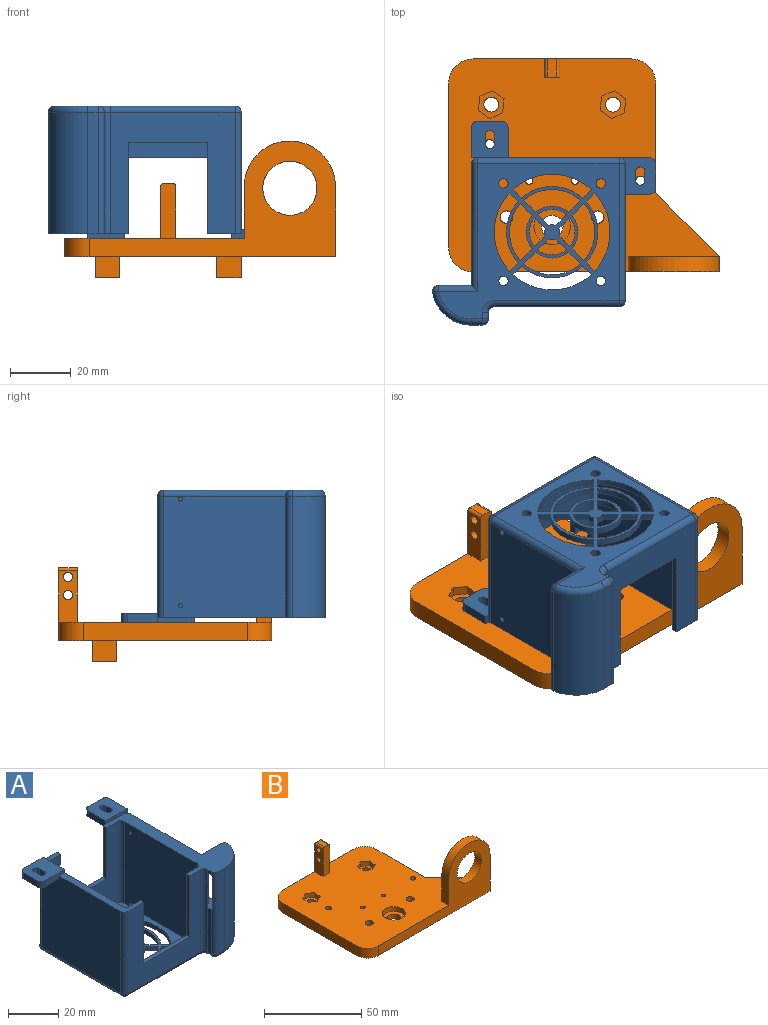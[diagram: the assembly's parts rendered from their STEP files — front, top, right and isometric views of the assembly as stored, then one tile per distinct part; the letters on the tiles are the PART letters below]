
ASSEMBLY  parts=2 mates=1
PART A: 150 faces, bbox 74.3x68.1x43.5 mm
  f0: plane 37x11mm, normal (0,0,1), area 127mm2, adj f2,f5,f73,f76,f84,f85,f121,f130
  f1: plane 7.89x3.33mm, normal (0,0,1), area 16.5mm2, adj f3,f8,f9,f119,f131
  f2: plane 41x40mm, normal (1,0,0), area 1628mm2, adj f0,f3,f70,f76,f130,f137
  f3: cylinder r=2mm len=40mm, axis (0,0,-1), area 113.9mm2, adj f1,f2,f6,f8,f70,f124,f131,f137
  f4: cylinder r=2mm len=38.5mm, axis (0,0,-1), area 121mm2, adj f5,f9,f109,f126
  f5: plane 45x40mm, normal (-1,0,0), area 1785mm2, adj f0,f4,f84,f107,f126,f130
  f6: plane 40x38mm, normal (0,-1,0), area 775.8mm2, adj f3,f7,f10,f70,f74,f117,f118,f123
  f7: plane 9x2mm, normal (1,0,0), area 18mm2, adj f6,f9,f117,f123
  f8: plane 6.5x6mm, normal (0,-1,0), area 31.8mm2, adj f1,f3,f119,f124,f125
  f9: plane 56.5x41.5mm, normal (0,1,0), area 1154.7mm2, adj f1,f4,f7,f10,f83,f111,f117,f118
  f10: plane 55x26.32mm, normal (0,0,1), area 467mm2, adj f6,f9,f15,f17,f72,f73,f74,f75
  f11: plane 11.87x1.77mm, normal (0,0,-1), area 21mm2, adj f12,f15,f81,f92,f94,f96
  f12: plane 31x11.54mm, normal (1,0,0), area 154.7mm2, adj f11,f88,f93,f94,f96,f100
  f13: plane 31x0.04mm, normal (0,1,0), area 1.2mm2, adj f91,f92,f93,f99
  f14: plane 10.82x2mm, normal (0,1,0), area 21.6mm2, adj f15,f82,f93,f116
  f15: cylinder r=2mm len=40mm, axis (0,0,-1), area 118.7mm2, adj f10,f11,f14,f80,f81,f92,f93,f114
  f16: plane 21.5x2mm, normal (-1,0,0), area 43mm2, adj f17,f77,f88,f106
  f17: cylinder r=2mm len=40mm, axis (0,0,-1), area 117.1mm2, adj f10,f16,f78,f79,f86,f87,f88,f108
  f18: plane 3.9x3.9mm, normal (0.71,0.71,0), area 11mm2, adj f19,f69,f70,f71
  f19: cylinder r=14mm len=18.71mm, axis (0,0,-1), area 41mm2, adj f18,f20,f70,f71
  f20: plane 3.9x3.9mm, normal (-0.71,0.71,0), area 11mm2, adj f19,f69,f70,f71
  f21: plane 2.83x2.83mm, normal (-0.71,0.71,0), area 8mm2, adj f22,f54,f70,f71
  f22: cylinder r=19mm len=25.79mm, axis (0,0,-1), area 56.7mm2, adj f21,f23,f70,f71
  f23: plane 2.83x2.83mm, normal (-0.71,-0.71,0), area 8mm2, adj f22,f54,f70,f71
  f24: plane 3.9x3.9mm, normal (-0.71,0.71,0), area 11mm2, adj f25,f55,f70,f71
  f25: cylinder r=14mm len=18.71mm, axis (0,0,-1), area 41mm2, adj f24,f26,f70,f71
  f26: plane 3.9x3.9mm, normal (-0.71,-0.71,0), area 11mm2, adj f25,f55,f70,f71
  f27: plane 3.9x3.9mm, normal (-0.71,-0.71,0), area 11mm2, adj f28,f56,f70,f71
  f28: cylinder r=14mm len=18.71mm, axis (0,0,-1), area 41mm2, adj f27,f29,f70,f71
  f29: plane 3.9x3.9mm, normal (0.71,-0.71,0), area 11mm2, adj f28,f56,f70,f71
  f30: cylinder r=15mm len=20.13mm, axis (0,0,-1), area 44.1mm2, adj f31,f61,f70,f71
  f31: plane 2.83x2.83mm, normal (-0.71,-0.71,0), area 8mm2, adj f30,f32,f70,f71
  f32: cylinder r=19mm len=25.79mm, axis (0,0,-1), area 56.7mm2, adj f31,f61,f70,f71
  f33: cylinder r=8.5mm len=10.91mm, axis (0,0,-1), area 23.7mm2, adj f34,f62,f70,f71
  f34: plane 3.9x3.9mm, normal (0.71,-0.71,0), area 11mm2, adj f33,f35,f70,f71
  f35: cylinder r=14mm len=18.71mm, axis (0,0,-1), area 41mm2, adj f34,f62,f70,f71
  f36: cylinder r=2.5mm len=2.31mm, axis (0,0,-1), area 4.8mm2, adj f37,f63,f70,f71
  f37: plane 3.59x3.59mm, normal (-0.71,0.71,0), area 10.2mm2, adj f36,f38,f70,f71
  f38: cylinder r=7.5mm len=9.49mm, axis (0,0,-1), area 20.6mm2, adj f37,f63,f70,f71
  f39: cylinder r=15mm len=20.13mm, axis (0,0,-1), area 44.1mm2, adj f40,f64,f70,f71
  f40: plane 2.83x2.83mm, normal (0.71,0.71,0), area 8mm2, adj f39,f41,f70,f71
  f41: cylinder r=19mm len=25.79mm, axis (0,0,-1), area 56.7mm2, adj f40,f64,f70,f71
  f42: cylinder r=2.5mm len=2.31mm, axis (0,0,-1), area 4.8mm2, adj f43,f65,f70,f71
  f43: plane 3.59x3.59mm, normal (0.71,0.71,0), area 10.2mm2, adj f42,f44,f70,f71
  f44: cylinder r=7.5mm len=9.49mm, axis (0,0,-1), area 20.6mm2, adj f43,f65,f70,f71
  f45: cylinder r=15mm len=20.13mm, axis (0,0,-1), area 44.1mm2, adj f46,f66,f70,f71
  f46: plane 2.83x2.83mm, normal (0.71,-0.71,0), area 8mm2, adj f45,f47,f70,f71
  f47: cylinder r=19mm len=25.79mm, axis (0,0,-1), area 56.7mm2, adj f46,f66,f70,f71
  f48: cylinder r=2.5mm len=2.31mm, axis (0,0,-1), area 4.8mm2, adj f49,f67,f70,f71
  f49: plane 3.59x3.59mm, normal (0.71,-0.71,0), area 10.2mm2, adj f48,f50,f70,f71
  f50: cylinder r=7.5mm len=9.49mm, axis (0,0,-1), area 20.6mm2, adj f49,f67,f70,f71
  f51: cylinder r=2.5mm len=2.31mm, axis (0,0,-1), area 4.8mm2, adj f52,f68,f70,f71
  f52: plane 3.59x3.59mm, normal (-0.71,-0.71,0), area 10.2mm2, adj f51,f53,f70,f71
  f53: cylinder r=7.5mm len=9.49mm, axis (0,0,-1), area 20.6mm2, adj f52,f68,f70,f71
  f54: cylinder r=15mm len=20.13mm, axis (0,0,-1), area 44.1mm2, adj f21,f23,f70,f71
  f55: cylinder r=8.5mm len=10.91mm, axis (0,0,-1), area 23.7mm2, adj f24,f26,f70,f71
  f56: cylinder r=8.5mm len=10.91mm, axis (0,0,-1), area 23.7mm2, adj f27,f29,f70,f71
  f57: cylinder r=1.55mm len=3.1mm, axis (0,0,-1), area 19.5mm2, adj f70,f71
  f58: cylinder r=1.55mm len=3.1mm, axis (0,0,-1), area 19.5mm2, adj f70,f71
  f59: cylinder r=1.55mm len=3.1mm, axis (0,0,-1), area 19.5mm2, adj f70,f71
  f60: cylinder r=1.55mm len=3.1mm, axis (0,0,-1), area 19.5mm2, adj f70,f71
  f61: plane 2.83x2.83mm, normal (0.71,-0.71,0), area 8mm2, adj f30,f32,f70,f71
  f62: plane 3.9x3.9mm, normal (0.71,0.71,0), area 11mm2, adj f33,f35,f70,f71
  f63: plane 3.59x3.59mm, normal (-0.71,-0.71,0), area 10.2mm2, adj f36,f38,f70,f71
  f64: plane 2.83x2.83mm, normal (-0.71,0.71,0), area 8mm2, adj f39,f41,f70,f71
  f65: plane 3.59x3.59mm, normal (-0.71,0.71,0), area 10.2mm2, adj f42,f44,f70,f71
  f66: plane 2.83x2.83mm, normal (0.71,0.71,0), area 8mm2, adj f45,f47,f70,f71
  f67: plane 3.59x3.59mm, normal (0.71,0.71,0), area 10.2mm2, adj f48,f50,f70,f71
  f68: plane 3.59x3.59mm, normal (0.71,-0.71,0), area 10.2mm2, adj f51,f53,f70,f71
  f69: cylinder r=8.5mm len=10.91mm, axis (0,0,-1), area 23.7mm2, adj f18,f20,f70,f71
  f70: plane 45x42mm, normal (0,0,1), area 970.5mm2, adj f2,f3,f6,f18,f19,f20,f21,f22
  f71: plane 59.32x51mm, normal (0,0,-1), area 1280mm2, adj f18,f19,f20,f21,f22,f23,f24,f25
  f72: plane 41x40mm, normal (-1,0,0), area 1636.9mm2, adj f10,f70,f74,f75,f101,f102
  f73: plane 40x38mm, normal (0,1,0), area 740mm2, adj f0,f10,f70,f75,f76,f120,f121,f122
  f74: cylinder r=2mm len=40mm, axis (0,0,-1), area 125.7mm2, adj f6,f10,f70,f72
  f75: cylinder r=2mm len=40mm, axis (0,0,-1), area 125.7mm2, adj f10,f70,f72,f73
  f76: cylinder r=2mm len=40mm, axis (0,0,-1), area 125.7mm2, adj f0,f2,f70,f73
  f77: cylinder r=2mm len=40mm, axis (0,0,-1), area 125.7mm2, adj f10,f16,f78,f85,f90,f104
  f78: plane 2x1.5mm, normal (-1,0,0), area 3mm2, adj f10,f17,f77,f87
  f79: plane 40x3.5mm, normal (0,-1,0), area 140mm2, adj f10,f17,f80,f110
  f80: cylinder r=13mm len=40mm, axis (0,0,-1), area 721.7mm2, adj f10,f15,f79,f112
  f81: plane 10.82x7mm, normal (0,1,0), area 75.7mm2, adj f10,f11,f15,f82
  f82: plane 40x40mm, normal (1,0,0), area 1596.9mm2, adj f10,f14,f81,f83,f94,f101,f102,f115
  f83: cylinder r=2mm len=40mm, axis (0,0,-1), area 125.7mm2, adj f9,f10,f82,f113,f141
  f84: cylinder r=2mm len=40mm, axis (0,0,-1), area 125.7mm2, adj f0,f5,f85,f105
  f85: plane 41x40mm, normal (0,-1,0), area 860mm2, adj f0,f10,f77,f84,f103,f120,f121,f122
  f86: plane 17x1.94mm, normal (0,1,0), area 33mm2, adj f17,f87,f88,f97
  f87: plane 17x9.86mm, normal (0,0,-1), area 128.3mm2, adj f17,f78,f86,f89,f90,f95,f96,f97
  f88: plane 9.86x6.99mm, normal (0,0,1), area 39mm2, adj f12,f16,f17,f86,f89,f90,f95,f96
  f89: plane 17x2mm, normal (0,-1,0), area 34mm2, adj f87,f88,f90,f95
  f90: plane 17x1.5mm, normal (1,0,0), area 25.5mm2, adj f77,f87,f88,f89
  f91: plane 0.23x0.04mm, normal (0,0,-1), area 0mm2, adj f13,f92,f99
  f92: plane 31x1.88mm, normal (-1,0,0), area 58.3mm2, adj f11,f13,f15,f91,f93
  f93: plane 11.87x2.24mm, normal (0,0,1), area 26.5mm2, adj f12,f13,f14,f15,f92,f94,f99,f100
  f94: plane 31x0.37mm, normal (0,-1,0), area 11.5mm2, adj f11,f12,f82,f93
  f95: plane 17x5.73mm, normal (1,0,0), area 97.4mm2, adj f87,f88,f89,f96
  f96: plane 17x15mm, normal (0,-1,0), area 118.5mm2, adj f11,f12,f87,f88,f95,f99
  f97: plane 17x0.13mm, normal (1,0,0), area 2.2mm2, adj f86,f87,f88,f98
  f98: plane 17x3.5mm, normal (0,1,0), area 59.4mm2, adj f87,f88,f97,f99
  f99: cylinder r=11.64mm len=36.5mm, axis (0,0,1), area 391.9mm2, adj f13,f87,f88,f91,f93,f96,f98,f100
  f100: plane 19.5x11.79mm, normal (0,0.9,0.43), area 194.7mm2, adj f12,f88,f93,f99
  f101: cylinder r=0.7mm len=5.5mm, axis (1,0,0), area 24.2mm2, adj f72,f82
  f102: cylinder r=0.7mm len=5.5mm, axis (1,0,0), area 24.2mm2, adj f72,f82
  f103: cylinder r=2mm len=41mm, axis (1,0,0), area 128.8mm2, adj f71,f85,f104,f105
  f104: torus R=4mm, axis (0,0,1), area 13.5mm2, adj f71,f77,f103,f106
  f105: sphere r=2mm, area 6.3mm2, adj f84,f103,f107
  f106: cylinder r=2mm len=2mm, axis (0,-1,0), area 6.3mm2, adj f16,f71,f104,f108
  f107: cylinder r=2mm len=45mm, axis (0,-1,0), area 141.4mm2, adj f5,f71,f105,f109
  f108: sphere r=2mm, area 6.3mm2, adj f17,f106,f110
  f109: sphere r=2mm, area 6.3mm2, adj f4,f107,f111
  f110: cylinder r=2mm len=3.5mm, axis (1,0,0), area 11mm2, adj f71,f79,f108,f112
  f111: cylinder r=2mm len=46.5mm, axis (-1,0,0), area 146.1mm2, adj f9,f71,f109,f113
  f112: torus R=11mm, axis (0,0,1), area 53.5mm2, adj f71,f80,f110,f114
  f113: sphere r=2mm, area 6.3mm2, adj f83,f111,f115
  f114: sphere r=2mm, area 7mm2, adj f15,f112,f116
  f115: cylinder r=2mm len=42mm, axis (0,1,0), area 127.9mm2, adj f71,f82,f113,f116
  f116: cylinder r=2mm len=12.82mm, axis (-1,0,0), area 36.3mm2, adj f14,f71,f114,f115
  f117: plane 26x2mm, normal (0,0,1), area 52mm2, adj f6,f7,f9,f118
  f118: plane 25x2mm, normal (-1,0,0), area 50mm2, adj f6,f9,f10,f117
  f119: plane 5x2mm, normal (1,0,0), area 10mm2, adj f1,f8,f9,f125
  f120: plane 30x2mm, normal (-1,0,0), area 60mm2, adj f10,f73,f85,f122
  f121: plane 30x2mm, normal (1,0,0), area 60mm2, adj f0,f73,f85,f122
  f122: plane 26x2mm, normal (0,0,1), area 52mm2, adj f73,f85,f120,f121
  f123: plane 2.22x2mm, normal (0,0,1), area 4.4mm2, adj f6,f7,f9,f124
  f124: cylinder r=5.5mm len=11mm, axis (0,1,0), area 38.8mm2, adj f3,f6,f8,f9,f123,f125
  f125: plane 2.22x2mm, normal (0,0,-1), area 4.4mm2, adj f8,f9,f119,f124
  f126: plane 12x12mm, normal (0,0,-1), area 103.1mm2, adj f4,f5,f9,f127,f128,f129,f130,f132
  f127: cylinder r=2mm len=3mm, axis (0,0,-1), area 9.4mm2, adj f9,f126,f128,f136
  f128: plane 8x3mm, normal (-1,0,0), area 24mm2, adj f126,f127,f129,f136
  f129: cylinder r=2mm len=3mm, axis (0,0,-1), area 9.4mm2, adj f126,f128,f130,f136
  f130: plane 11.11x3mm, normal (0,-1,0), area 28.8mm2, adj f0,f2,f5,f126,f129,f131,f136,f137
  f131: plane 12x3mm, normal (1,0,0), area 31mm2, adj f1,f3,f9,f130,f136,f137
  f132: plane 3x3mm, normal (1,0,0), area 9mm2, adj f126,f133,f135,f136
  f133: cylinder r=1.5mm len=3mm, axis (0,0,-1), area 14.1mm2, adj f126,f132,f134,f136
  f134: plane 3x3mm, normal (-1,0,0), area 9mm2, adj f126,f133,f135,f136
  f135: cylinder r=1.5mm len=3mm, axis (0,0,-1), area 14.1mm2, adj f126,f132,f134,f136
  f136: plane 13.11x12mm, normal (0,0,1), area 139.6mm2, adj f9,f127,f128,f129,f130,f131,f132,f133
  f137: plane 8.67x0.11mm, normal (0,0,-1), area 1mm2, adj f2,f3,f130,f131
  f138: cylinder r=1.5mm len=3mm, axis (0,0,-1), area 14.1mm2, adj f139,f147,f148,f149
  f139: plane 3x3mm, normal (-1,0,0), area 9mm2, adj f138,f140,f148,f149
  f140: cylinder r=1.5mm len=3mm, axis (0,0,-1), area 14.1mm2, adj f139,f147,f148,f149
  f141: plane 12x3mm, normal (0,-1,0), area 21mm2, adj f10,f83,f142,f146,f148,f149
  f142: plane 10x3mm, normal (1,0,0), area 30mm2, adj f141,f143,f148,f149
  f143: cylinder r=2mm len=3mm, axis (0,0,-1), area 9.4mm2, adj f142,f144,f148,f149
  f144: plane 8x3mm, normal (0,1,0), area 24mm2, adj f143,f145,f148,f149
  f145: cylinder r=2mm len=3mm, axis (0,0,-1), area 9.4mm2, adj f144,f146,f148,f149
  f146: plane 10x3mm, normal (-1,0,0), area 30mm2, adj f9,f141,f145,f148,f149
  f147: plane 3x3mm, normal (1,0,0), area 9mm2, adj f138,f140,f148,f149
  f148: plane 12x12mm, normal (0,0,1), area 126.2mm2, adj f138,f139,f140,f141,f142,f143,f144,f145
  f149: plane 12x12mm, normal (0,0,-1), area 126.2mm2, adj f9,f138,f139,f140,f141,f142,f143,f144
PART B: 86 faces, bbox 89x70x45 mm
  f0: plane 89x70mm, normal (0,0,1), area 4590.8mm2, adj f1,f2,f4,f5,f6,f7,f8,f9
  f1: cylinder r=2.05mm len=4.1mm, axis (0,0,-1), area 38.6mm2, adj f0,f75
  f2: cylinder r=2.05mm len=4.1mm, axis (0,0,-1), area 38.6mm2, adj f0,f68
  f3: plane 89x70mm, normal (0,0,-1), area 4729.8mm2, adj f6,f7,f8,f9,f10,f11,f12,f13
  f4: cylinder r=1.5mm len=3mm, axis (0,0,1), area 28.3mm2, adj f0,f36
  f5: cylinder r=1.5mm len=3mm, axis (0,0,1), area 28.3mm2, adj f0,f43
  f6: plane 52x24mm, normal (0,1,0), area 401.6mm2, adj f0,f3,f7,f16,f50,f52,f53,f56
  f7: cylinder r=8mm len=8mm, axis (0,0,1), area 75.4mm2, adj f0,f3,f6,f8
  f8: plane 54x6mm, normal (-1,0,0), area 324mm2, adj f0,f3,f7,f9
  f9: cylinder r=8mm len=8mm, axis (0,0,1), area 75.4mm2, adj f0,f3,f8,f10
  f10: plane 81x38mm, normal (0,-1,0), area 1100.6mm2, adj f0,f3,f9,f11,f83,f84,f85
  f11: plane 23x5mm, normal (1,0,0), area 115mm2, adj f3,f10,f12,f82,f85
  f12: plane 21x21mm, normal (0.71,0.71,0), area 178.2mm2, adj f0,f3,f11,f13
  f13: plane 36x6mm, normal (1,0,0), area 216mm2, adj f0,f3,f12,f16
  f14: cylinder r=1.2mm len=6mm, axis (0,0,1), area 45.2mm2, adj f0,f3
  f15: cylinder r=1.2mm len=6mm, axis (0,0,1), area 45.2mm2, adj f0,f3
  f16: cylinder r=8mm len=8mm, axis (0,0,1), area 75.4mm2, adj f0,f3,f6,f13
  f17: cylinder r=6mm len=12mm, axis (0,0,1), area 113.1mm2, adj f0,f18
  f18: plane 12x12mm, normal (0,0,1), area 72.9mm2, adj f17,f35
  f19: plane 4.6x3mm, normal (-0.99,0.1,0), area 13.9mm2, adj f0,f20,f24,f25
  f20: plane 3.74x3mm, normal (-0.59,-0.81,0), area 13.9mm2, adj f0,f19,f21,f25
  f21: plane 4.21x3mm, normal (0.41,-0.91,0), area 13.9mm2, adj f0,f20,f22,f25
  f22: plane 4.6x3mm, normal (0.99,-0.1,0), area 13.9mm2, adj f0,f21,f23,f25
  f23: plane 3.74x3mm, normal (0.59,0.81,0), area 13.9mm2, adj f0,f22,f24,f25
  f24: plane 4.21x3mm, normal (-0.41,0.91,0), area 13.9mm2, adj f0,f19,f23,f25
  f25: plane 9.19x8.43mm, normal (0,0,1), area 36.6mm2, adj f19,f20,f21,f22,f23,f24,f34
  f26: plane 3.74x3mm, normal (-0.59,-0.81,0), area 13.9mm2, adj f0,f27,f31,f32
  f27: plane 4.21x3mm, normal (0.41,-0.91,0), area 13.9mm2, adj f0,f26,f28,f32
  f28: plane 4.6x3mm, normal (0.99,-0.1,0), area 13.9mm2, adj f0,f27,f29,f32
  f29: plane 3.74x3mm, normal (0.59,0.81,0), area 13.9mm2, adj f0,f28,f30,f32
  f30: plane 4.21x3mm, normal (-0.41,0.91,0), area 13.9mm2, adj f0,f29,f31,f32
  f31: plane 4.6x3mm, normal (-0.99,0.1,0), area 13.9mm2, adj f0,f26,f30,f32
  f32: plane 9.19x8.43mm, normal (0,0,1), area 36.6mm2, adj f26,f27,f28,f29,f30,f31,f33
  f33: cylinder r=2.45mm len=10mm, axis (0,0,1), area 153.9mm2, adj f32,f58
  f34: cylinder r=2.45mm len=10mm, axis (0,0,1), area 153.9mm2, adj f25,f67
  f35: cylinder r=3.58mm len=7.15mm, axis (0,0,1), area 67.4mm2, adj f3,f18
  f36: plane 6.35x5.5mm, normal (0,0,-1), area 19.1mm2, adj f4,f37,f38,f39,f40,f41,f42
  f37: plane 3x2.75mm, normal (-0.87,0.5,0), area 9.5mm2, adj f3,f36,f38,f42
  f38: plane 3.18x3mm, normal (0,1,0), area 9.5mm2, adj f3,f36,f37,f39
  f39: plane 3x2.75mm, normal (0.87,0.5,0), area 9.5mm2, adj f3,f36,f38,f40
  f40: plane 3x2.75mm, normal (0.87,-0.5,0), area 9.5mm2, adj f3,f36,f39,f41
  f41: plane 3.18x3mm, normal (0,-1,0), area 9.5mm2, adj f3,f36,f40,f42
  f42: plane 3x2.75mm, normal (-0.87,-0.5,0), area 9.5mm2, adj f3,f36,f37,f41
  f43: plane 6.35x5.5mm, normal (0,0,-1), area 19.1mm2, adj f5,f44,f45,f46,f47,f48,f49
  f44: plane 3x2.75mm, normal (0.87,-0.5,0), area 9.5mm2, adj f3,f43,f45,f49
  f45: plane 3.18x3mm, normal (0,-1,0), area 9.5mm2, adj f3,f43,f44,f46
  f46: plane 3x2.75mm, normal (-0.87,-0.5,0), area 9.5mm2, adj f3,f43,f45,f47
  f47: plane 3x2.75mm, normal (-0.87,0.5,0), area 9.5mm2, adj f3,f43,f46,f48
  f48: plane 3.18x3mm, normal (0,1,0), area 9.5mm2, adj f3,f43,f47,f49
  f49: plane 3x2.75mm, normal (0.87,0.5,0), area 9.5mm2, adj f3,f43,f44,f48
  f50: plane 17x6mm, normal (-1,0,0), area 87.9mm2, adj f0,f6,f51,f54,f55,f56
  f51: plane 18x5mm, normal (0,-1,0), area 89.6mm2, adj f0,f50,f52,f53,f56,f57
  f52: plane 17x6mm, normal (1,0,0), area 87.9mm2, adj f0,f6,f51,f54,f55,f57
  f53: plane 6x3mm, normal (0,0,1), area 18mm2, adj f6,f51,f56,f57
  f54: cylinder r=1.5mm len=5mm, axis (1,0,0), area 47.1mm2, adj f50,f52
  f55: cylinder r=1.5mm len=5mm, axis (1,0,0), area 47.1mm2, adj f50,f52
  f56: cylinder r=1mm len=6mm, axis (0,1,0), area 9.4mm2, adj f6,f50,f51,f53
  f57: cylinder r=1mm len=6mm, axis (0,-1,0), area 9.4mm2, adj f6,f51,f52,f53
  f58: plane 8x8mm, normal (0,0,-1), area 45.1mm2, adj f33,f59,f60,f61,f62
  f59: plane 8x7mm, normal (0,1,0), area 56mm2, adj f3,f58,f60,f62
  f60: plane 8x7mm, normal (-1,0,0), area 56mm2, adj f3,f58,f59,f61
  f61: plane 8x7mm, normal (0,-1,0), area 56mm2, adj f3,f58,f60,f62
  f62: plane 8x7mm, normal (1,0,0), area 56mm2, adj f3,f58,f59,f61
  f63: plane 8x7mm, normal (1,0,0), area 56mm2, adj f3,f64,f66,f67
  f64: plane 8x7mm, normal (0,-1,0), area 56mm2, adj f3,f63,f65,f67
  f65: plane 8x7mm, normal (-1,0,0), area 56mm2, adj f3,f64,f66,f67
  f66: plane 8x7mm, normal (0,1,0), area 56mm2, adj f3,f63,f65,f67
  f67: plane 8x8mm, normal (0,0,-1), area 45.1mm2, adj f34,f63,f64,f65,f66
  f68: plane 8.08x7mm, normal (0,0,-1), area 29.2mm2, adj f2,f69,f70,f71,f72,f73,f74
  f69: plane 3.5x3mm, normal (-0.87,0.5,0), area 12.1mm2, adj f3,f68,f70,f74
  f70: plane 4.04x3mm, normal (0,1,0), area 12.1mm2, adj f3,f68,f69,f71
  f71: plane 3.5x3mm, normal (0.87,0.5,0), area 12.1mm2, adj f3,f68,f70,f72
  f72: plane 3.5x3mm, normal (0.87,-0.5,0), area 12.1mm2, adj f3,f68,f71,f73
  f73: plane 4.04x3mm, normal (0,-1,0), area 12.1mm2, adj f3,f68,f72,f74
  f74: plane 3.5x3mm, normal (-0.87,-0.5,0), area 12.1mm2, adj f3,f68,f69,f73
  f75: plane 8.08x7mm, normal (0,0,-1), area 29.2mm2, adj f1,f76,f77,f78,f79,f80,f81
  f76: plane 3.5x3mm, normal (-0.87,0.5,0), area 12.1mm2, adj f3,f75,f77,f81
  f77: plane 4.04x3mm, normal (0,1,0), area 12.1mm2, adj f3,f75,f76,f78
  f78: plane 3.5x3mm, normal (0.87,0.5,0), area 12.1mm2, adj f3,f75,f77,f79
  f79: plane 3.5x3mm, normal (0.87,-0.5,0), area 12.1mm2, adj f3,f75,f78,f80
  f80: plane 4.04x3mm, normal (0,-1,0), area 12.1mm2, adj f3,f75,f79,f81
  f81: plane 3.5x3mm, normal (-0.87,-0.5,0), area 12.1mm2, adj f3,f75,f76,f80
  f82: plane 32x30mm, normal (0,1,0), area 614.6mm2, adj f0,f11,f83,f84,f85
  f83: plane 17x5mm, normal (-1,0,0), area 85mm2, adj f0,f10,f82,f85
  f84: cylinder r=8.9mm len=17.8mm, axis (0,-1,0), area 279.6mm2, adj f10,f82
  f85: cylinder r=15mm len=30mm, axis (0,1,0), area 235.6mm2, adj f10,f11,f82,f83
PLACE A rot(axis=(0,1,0),180deg) t=(22.13,-14.61,56.92)mm
PLACE B t=(-11.87,-5.11,13.42)mm fixed
MATE fastened A.f135 <-> B.f4  axis (0,0,-1) through (51.13,24.89,13.42)mm
